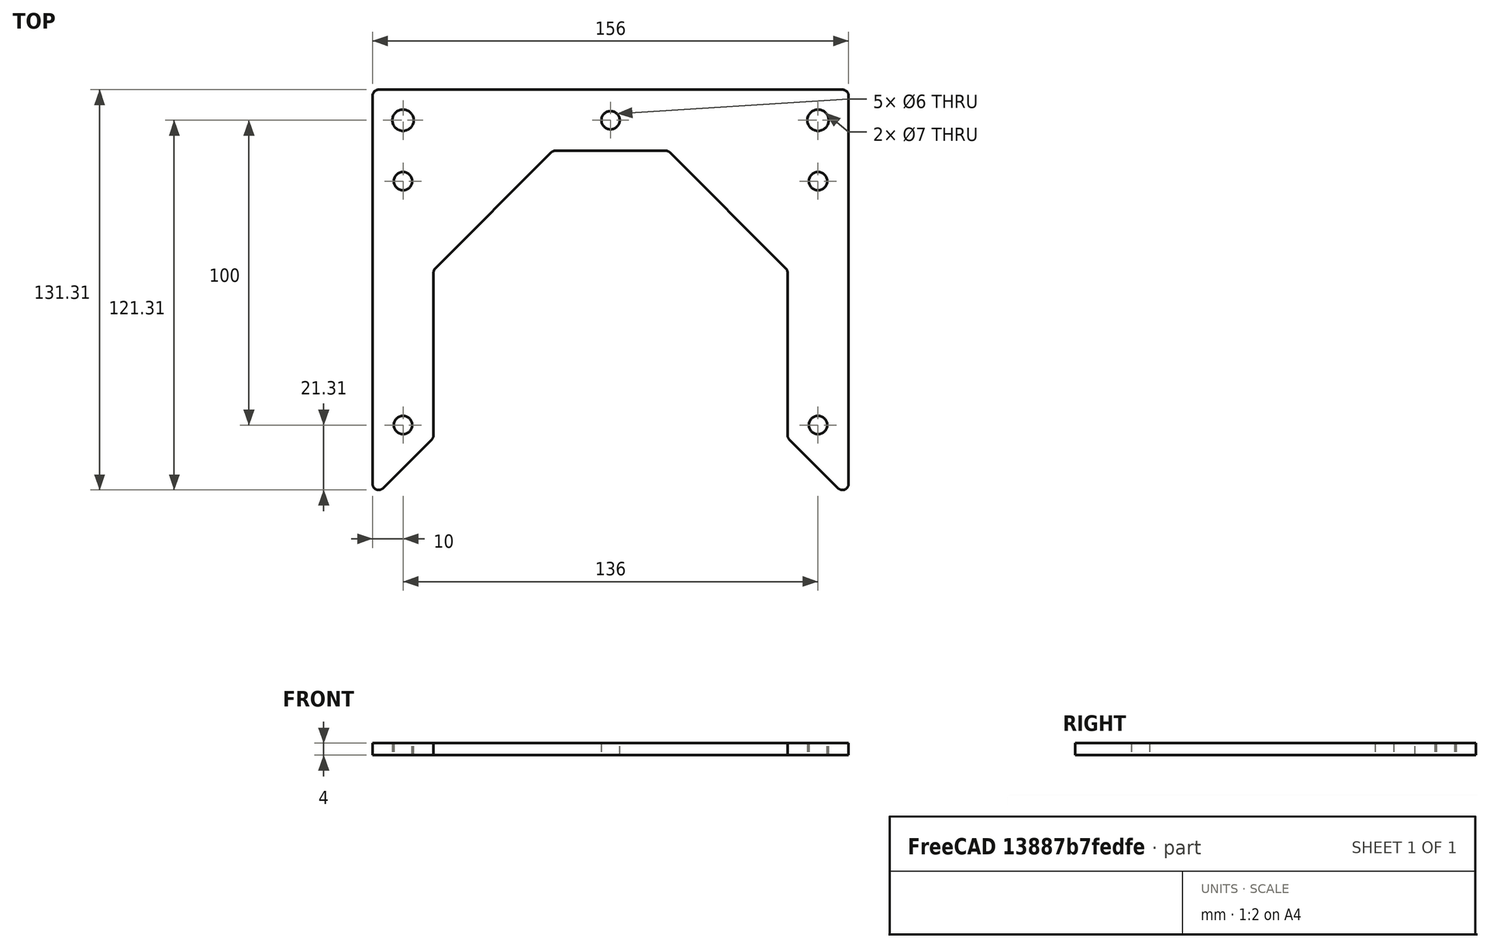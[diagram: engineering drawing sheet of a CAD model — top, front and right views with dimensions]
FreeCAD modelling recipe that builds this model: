
FCSTD DOCUMENT  (FreeCAD 0.19R24267 +99 (Git))
Label: V2 Enclosure ends U bracket with rail end holes
License: All rights reserved
LicenseURL: http://en.wikipedia.org/wiki/All_rights_reserved
objects: Sketcher::SketchObject×1, PartDesign::Pad×1, PartDesign::Body×1
note: 4 computed .brp shape members not serialized (recipe doc carries the construction recipe); baked Part::Feature solids carry a one-line shape summary decoded from their .brp

FEATURE [Sketcher::SketchObject] Sketch
  FullyConstrained = true
  MapMode = 5
  Support = -> [XY_Plane]
  sketch-geometry (33):
    g0: Circle CenterX=-68 CenterY=0 CenterZ=0 NormalX=0 NormalY=0 NormalZ=1 AngleXU=0 Radius=3.5
    g1: Circle CenterX=68 CenterY=0 CenterZ=0 NormalX=0 NormalY=0 NormalZ=1 AngleXU=0 Radius=3.5
    g2: LineSegment StartX=-68 StartY=0 StartZ=0 EndX=-68 EndY=-114.142 EndZ=0
    g3: Circle CenterX=-68 CenterY=-20 CenterZ=0 NormalX=0 NormalY=0 NormalZ=1 AngleXU=0 Radius=3
    g4: Circle CenterX=-68 CenterY=-100 CenterZ=0 NormalX=0 NormalY=0 NormalZ=1 AngleXU=0 Radius=3
    g5: LineSegment StartX=68 StartY=0 StartZ=0 EndX=68 EndY=-114.142 EndZ=0
    g6: Circle CenterX=68 CenterY=-20 CenterZ=0 NormalX=0 NormalY=0 NormalZ=1 AngleXU=0 Radius=3
    g7: Circle CenterX=68 CenterY=-100 CenterZ=0 NormalX=0 NormalY=0 NormalZ=1 AngleXU=0 Radius=3
    g8: LineSegment StartX=-78 StartY=8 StartZ=0 EndX=-78 EndY=-119.314 EndZ=0
    g9: LineSegment StartX=-58 StartY=-50 StartZ=0 EndX=-58 EndY=-103.314 EndZ=0
    g10: LineSegment StartX=-57.4142 StartY=-48.5858 StartZ=0 EndX=-19.4142 EndY=-10.5858 EndZ=0
    g11: LineSegment StartX=-18 StartY=-10 StartZ=0 EndX=18 EndY=-10 EndZ=0
    g12: LineSegment StartX=19.4142 StartY=-10.5858 StartZ=0 EndX=57.4142 EndY=-48.5858 EndZ=0
    g13: LineSegment StartX=58 StartY=-50 StartZ=0 EndX=58 EndY=-103.314 EndZ=0
    g14: LineSegment StartX=58.5858 StartY=-104.728 StartZ=0 EndX=74.5858 EndY=-120.728 EndZ=0
    g15: LineSegment StartX=78 StartY=-119.314 StartZ=0 EndX=78 EndY=8 EndZ=0
    g16: LineSegment StartX=76 StartY=10 StartZ=0 EndX=-76 EndY=10 EndZ=0
    g17: LineSegment StartX=-74.5858 StartY=-120.728 StartZ=0 EndX=-58.5858 EndY=-104.728 EndZ=0
    g18: ArcOfCircle CenterX=-76 CenterY=8 CenterZ=0 NormalX=0 NormalY=0 NormalZ=1 AngleXU=0 Radius=2 StartAngle=1.5708 EndAngle=3.14159
    g19: ArcOfCircle CenterX=-76 CenterY=-119.314 CenterZ=0 NormalX=0 NormalY=0 NormalZ=1 AngleXU=0 Radius=2 StartAngle=3.14159 EndAngle=5.49779
    g20: ArcOfCircle CenterX=-60 CenterY=-103.314 CenterZ=0 NormalX=0 NormalY=0 NormalZ=1 AngleXU=0 Radius=2 StartAngle=5.49779 EndAngle=6.28319
    g21: ArcOfCircle CenterX=60 CenterY=-103.314 CenterZ=0 NormalX=0 NormalY=0 NormalZ=1 AngleXU=0 Radius=2 StartAngle=3.14159 EndAngle=3.92699
    g22: ArcOfCircle CenterX=76 CenterY=-119.314 CenterZ=0 NormalX=0 NormalY=0 NormalZ=1 AngleXU=0 Radius=2 StartAngle=3.92699 EndAngle=6.28319
    g23: ArcOfCircle CenterX=76 CenterY=8 CenterZ=0 NormalX=0 NormalY=0 NormalZ=1 AngleXU=0 Radius=2 StartAngle=0 EndAngle=1.5708
    g24: ArcOfCircle CenterX=-56 CenterY=-50 CenterZ=0 NormalX=0 NormalY=0 NormalZ=1 AngleXU=0 Radius=2 StartAngle=2.35619 EndAngle=3.14159
    g25: ArcOfCircle CenterX=-18 CenterY=-12 CenterZ=0 NormalX=0 NormalY=0 NormalZ=1 AngleXU=0 Radius=2 StartAngle=1.5708 EndAngle=2.35619
    g26: ArcOfCircle CenterX=18 CenterY=-12 CenterZ=0 NormalX=0 NormalY=0 NormalZ=1 AngleXU=0 Radius=2 StartAngle=0.785398 EndAngle=1.5708
    g27: ArcOfCircle CenterX=56 CenterY=-50 CenterZ=0 NormalX=0 NormalY=0 NormalZ=1 AngleXU=0 Radius=2 StartAngle=0 EndAngle=0.785398
    g28: Circle CenterX=-68 CenterY=-100 CenterZ=0 NormalX=0 NormalY=0 NormalZ=1 AngleXU=0 Radius=10
    g29: Circle CenterX=68 CenterY=-100 CenterZ=0 NormalX=0 NormalY=0 NormalZ=1 AngleXU=0 Radius=10
    g30: GeomPoint X=0 Y=-10 Z=0
    g31: GeomPoint X=0 Y=10 Z=0
    g32: Circle CenterX=0 CenterY=0 CenterZ=0 NormalX=0 NormalY=0 NormalZ=1 AngleXU=0 Radius=3
  constraints (77):
    c: PointOnObject(g0,g-1)
    c: Symmetric(g0,g1,g-2)
    c: Coincident(g2,g0)
    c: Vertical(g2)
    c: PointOnObject(g3,g2)
    c: PointOnObject(g4,g2)
    c: Coincident(g5,g1)
    c: Vertical(g5)
    c: Symmetric(g3,g6,g-2)
    c: Symmetric(g4,g7,g-2)
    c: DistanceX(g0,g1) = 136
    c: Equal(g4,g3)
    c: Equal(g3,g6)
    c: Equal(g6,g7)
    c: Radius(g3) = 3
    c: Radius(g0) = 3.5
    c: Vertical(g8)
    c: Vertical(g9)
    c: Vertical(g15)
    c: Horizontal(g16)
    c: Tangent(g16,g18) = -1.5708
    c: Tangent(g8,g18) = -1.5708
    c: Tangent(g8,g19) = -1.5708
    c: Tangent(g17,g19) = -1.5708
    c: Tangent(g9,g20) = 1.5708
    c: Tangent(g17,g20) = -1.5708
    c: Tangent(g13,g21) = -1.5708
    c: Tangent(g14,g21) = -1.5708
    c: Tangent(g15,g22) = -1.5708
    c: Tangent(g14,g22) = -1.5708
    c: Tangent(g16,g23) = -1.5708
    c: Tangent(g15,g23) = -1.5708
    c: Tangent(g10,g24) = 1.5708
    c: Tangent(g9,g24) = -1.5708
    c: Tangent(g10,g25) = 1.5708
    c: Tangent(g11,g25) = 1.5708
    c: Tangent(g12,g26) = 1.5708
    c: Tangent(g11,g26) = 1.5708
    c: Tangent(g12,g27) = 1.5708
    c: Tangent(g13,g27) = 1.5708
    c: Equal(g18,g24)
    c: Equal(g24,g25)
    c: Equal(g25,g23)
    c: Equal(g23,g26)
    c: Equal(g26,g27)
    c: Equal(g27,g22)
    c: Equal(g22,g21)
    c: Equal(g21,g19)
    c: Equal(g19,g20)
    c: Radius(g18) = 2
    c: PointOnObject(g2,g17)
    c: PointOnObject(g5,g14)
    c: Coincident(g28,g4)
    c: Coincident(g29,g7)
    c: Tangent(g29,g15)
    c: Tangent(g29,g14)
    c: Tangent(g13,g29)
    c: Tangent(g8,g28)
    c: Angle(g17,g8) = 0.785398
    c: DistanceX(g9,g11) = 40
    c: DistanceY(g9,g11) = 40
    c: Symmetric(g11,g11,g-2)
    c: Symmetric(g9,g13,g-2)
    c: DistanceX(g8,g9) = 20
    c: Symmetric(g8,g15,g-2)
    c: Symmetric(g9,g13,g-2)
    c: PointOnObject(g30,g-2)
    c: PointOnObject(g30,g11)
    c: PointOnObject(g31,g16)
    c: Symmetric(g31,g30,g-1)
    c: DistanceY(g30,g31) = 20
    c: Equal(g1,g0)
    c: DistanceY(g3,g0) = 20
    c: DistanceY(g4,g0) = 100
    c: Coincident(g32,g-1)
    c: Equal(g32,g3)
    c: Diameter(g32) = 6
FEATURE [PartDesign::Pad] Pad
  Direction = (1,1,1)
  Length = 4
  Length2 = 100
  Profile = -> Sketch
  Type = 0
FEATURE [PartDesign::Body] Body
  Group = -> [Sketch,Pad]
  Origin = -> Origin
  Tip = -> Pad
